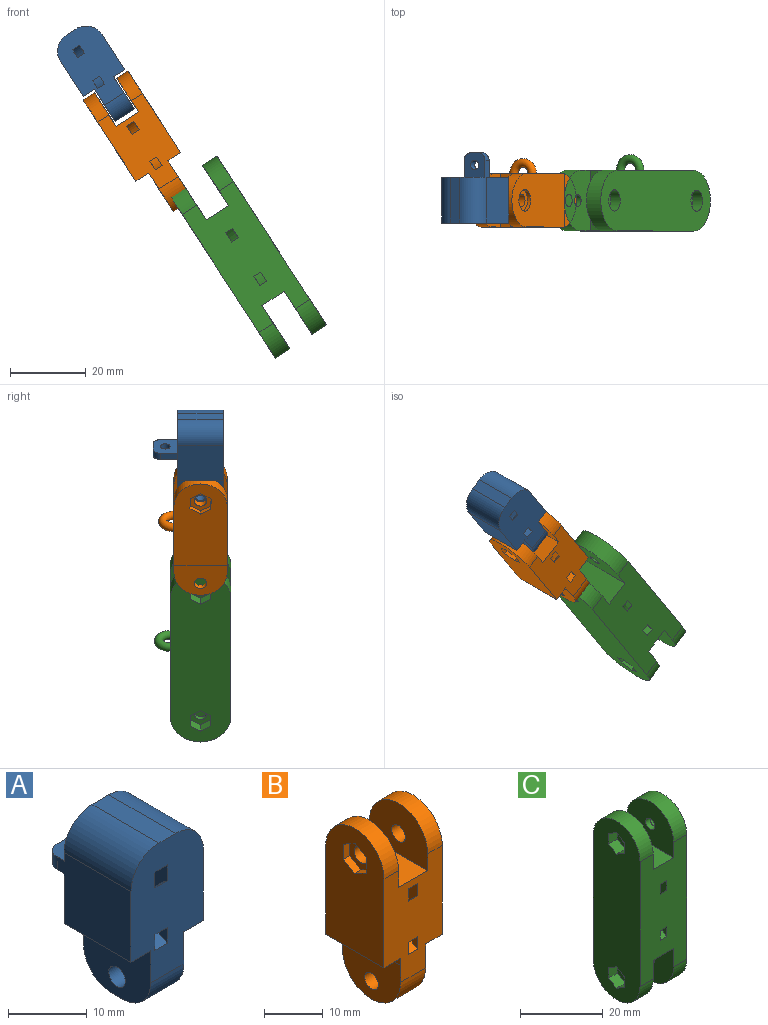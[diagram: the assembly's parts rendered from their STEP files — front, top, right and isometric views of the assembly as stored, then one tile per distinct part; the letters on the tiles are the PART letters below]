
ASSEMBLY  parts=3 mates=1
PART A: 27 faces, bbox 13x18.5x26 mm
  f0: plane 21x13mm, normal (0,-1,0), area 216.5mm2, adj f3,f4,f5,f6,f7,f8,f9,f11
  f1: plane 6x2mm, normal (0,0,-1), area 12mm2, adj f6,f9,f13,f14
  f2: plane 21x13mm, normal (0,1,0), area 214.3mm2, adj f3,f4,f5,f6,f7,f8,f9,f11
  f3: plane 12x11mm, normal (1,0,0), area 132mm2, adj f0,f2,f8,f12
  f4: plane 12x11mm, normal (-1,0,0), area 132mm2, adj f0,f2,f7,f11
  f5: plane 12x3mm, normal (0,0,1), area 36mm2, adj f0,f2,f11,f12
  f6: plane 12x10mm, normal (-1,0,0), area 102.2mm2, adj f0,f1,f2,f7,f10,f13,f14
  f7: plane 12x3.5mm, normal (0,0,-1), area 42mm2, adj f0,f2,f4,f6
  f8: plane 12x3.5mm, normal (0,0,-1), area 42mm2, adj f0,f2,f3,f9
  f9: plane 12x10mm, normal (1,0,0), area 102.2mm2, adj f0,f1,f2,f8,f10,f13,f14
  f10: cylinder r=1.5mm len=6mm, axis (-1,0,0), area 56.5mm2, adj f6,f9
  f11: cylinder r=5mm len=12mm, axis (0,-1,0), area 94.2mm2, adj f0,f2,f4,f5
  f12: cylinder r=5mm len=12mm, axis (0,1,0), area 94.2mm2, adj f0,f2,f3,f5
  f13: cylinder r=5mm len=6mm, axis (1,0,0), area 47.1mm2, adj f1,f2,f6,f9
  f14: cylinder r=5mm len=6mm, axis (1,0,0), area 47.1mm2, adj f0,f1,f6,f9
  f15: plane 6.5x6.5mm, normal (0,0,-1), area 35.6mm2, adj f2,f16,f18,f19,f20,f21,f22
  f16: plane 4.5x2mm, normal (-1,0,0), area 9mm2, adj f2,f15,f17,f22
  f17: plane 6.5x6.5mm, normal (0,0,1), area 35.6mm2, adj f2,f16,f18,f19,f20,f21,f22
  f18: plane 4.5x2mm, normal (1,0,0), area 9mm2, adj f2,f15,f17,f21
  f19: plane 2.5x2mm, normal (0,1,0), area 5mm2, adj f15,f17,f21,f22
  f20: cylinder r=1.25mm len=2.5mm, axis (0,0,-1), area 15.7mm2, adj f15,f17
  f21: cylinder r=2mm len=2mm, axis (0,0,1), area 6.3mm2, adj f15,f17,f18,f19
  f22: cylinder r=2mm len=2mm, axis (0,0,-1), area 6.3mm2, adj f15,f16,f17,f19
  f23: cylinder r=6.5mm len=12.16mm, axis (1,0,0), area 34.6mm2, adj f0,f25,f26
  f24: cylinder r=4.3mm len=7.27mm, axis (1,0,0), area 19mm2, adj f0,f25,f26
  f25: plane 12.16x4.2mm, normal (1,0,0), area 26.8mm2, adj f0,f23,f24
  f26: plane 12.16x4.2mm, normal (-1,0,0), area 26.8mm2, adj f0,f23,f24
PART B: 33 faces, bbox 14x18.3x37.5 mm
  f0: plane 25.49x14mm, normal (-1,0,0), area 309.6mm2, adj f11,f13,f14,f16,f22,f23,f24,f25
  f1: cylinder r=1.65mm len=3.3mm, axis (1,0,0), area 20.7mm2, adj f10,f21
  f2: cylinder r=1.65mm len=3.3mm, axis (1,0,0), area 25.9mm2, adj f8,f19
  f3: plane 14x10.5mm, normal (-1,0,0), area 117.4mm2, adj f12,f13,f14,f15,f18
  f4: plane 14x10.47mm, normal (1,0,0), area 117mm2, adj f5,f13,f14,f15,f18
  f5: plane 14x1.5mm, normal (1,0,-0.01), area 21mm2, adj f4,f6,f13,f14
  f6: plane 14x4mm, normal (0,0,-1), area 56mm2, adj f5,f7,f13,f14
  f7: plane 25.52x14mm, normal (1,0,0), area 310.8mm2, adj f6,f13,f14,f17,f20
  f8: plane 14x10.51mm, normal (-1,0,0), area 117.5mm2, adj f2,f9,f13,f14,f17
  f9: plane 14x7mm, normal (0,0,1), area 98mm2, adj f8,f10,f13,f14
  f10: plane 14x10.51mm, normal (1,0,0), area 117.5mm2, adj f1,f9,f13,f14,f16
  f11: plane 14x4mm, normal (0,0,-1), area 56mm2, adj f0,f12,f13,f14
  f12: plane 14x1.5mm, normal (-1,0,0.01), area 21mm2, adj f3,f11,f13,f14
  f13: plane 23.49x14mm, normal (0,-1,0), area 253.3mm2, adj f0,f3,f4,f5,f6,f7,f8,f9
  f14: plane 23.49x14mm, normal (0,1,0), area 256.5mm2, adj f0,f3,f4,f5,f6,f7,f8,f9
  f15: cylinder r=1.65mm len=6mm, axis (1,0,0), area 62.2mm2, adj f3,f4
  f16: cylinder r=7mm len=14mm, axis (1,0,0), area 77mm2, adj f0,f10,f13,f14
  f17: cylinder r=7mm len=14mm, axis (1,0,0), area 77mm2, adj f7,f8,f13,f14
  f18: cylinder r=7mm len=14mm, axis (-1,0,0), area 131.9mm2, adj f3,f4,f13,f14
  f19: plane 5.7x5.7mm, normal (1,0,0), area 17mm2, adj f2,f20
  f20: cylinder r=2.85mm len=5.7mm, axis (1,0,0), area 17.9mm2, adj f7,f19
  f21: plane 6.35x5.57mm, normal (-1,0,0), area 17.7mm2, adj f1,f22,f23,f24,f25,f26,f27
  f22: plane 3.18x1.5mm, normal (0,1,0.02), area 4.8mm2, adj f0,f21,f23,f27
  f23: plane 2.72x1.65mm, normal (0,0.52,-0.86), area 4.8mm2, adj f0,f21,f22,f24
  f24: plane 2.78x1.53mm, normal (0,-0.48,-0.88), area 4.8mm2, adj f0,f21,f23,f25
  f25: plane 3.18x1.5mm, normal (0,-1,-0.02), area 4.8mm2, adj f0,f21,f24,f26
  f26: plane 2.72x1.65mm, normal (0,-0.52,0.86), area 4.8mm2, adj f0,f21,f25,f27
  f27: plane 2.78x1.53mm, normal (0,0.48,0.88), area 4.8mm2, adj f0,f21,f22,f26
  f28: torus R=2.89mm, axis (0,0,1), area 64.2mm2, adj f14
  f29: cylinder r=7.5mm len=13.66mm, axis (1,0,0), area 37.8mm2, adj f13,f31,f32
  f30: cylinder r=5.3mm len=8.6mm, axis (1,0,0), area 22.1mm2, adj f13,f31,f32
  f31: plane 13.66x4.4mm, normal (1,0,0), area 30mm2, adj f13,f29,f30
  f32: plane 13.66x4.4mm, normal (-1,0,0), area 30mm2, adj f13,f29,f30
PART C: 41 faces, bbox 16x20.5x53 mm
  f0: plane 53x16mm, normal (-1,0,0), area 740.7mm2, adj f12,f13,f16,f17,f22,f23,f24,f25
  f1: cylinder r=1.55mm len=3.1mm, axis (1,0,0), area 14.6mm2, adj f11,f29
  f2: cylinder r=1.55mm len=3.1mm, axis (1,0,0), area 14.6mm2, adj f6,f28
  f3: plane 53x16mm, normal (1,0,0), area 743.8mm2, adj f12,f13,f14,f15,f18,f21
  f4: cylinder r=1.55mm len=3.1mm, axis (1,0,0), area 14.6mm2, adj f9,f20
  f5: cylinder r=1.55mm len=3.1mm, axis (1,0,0), area 14.6mm2, adj f8,f19
  f6: plane 16x13.5mm, normal (1,0,0), area 181mm2, adj f2,f7,f12,f13,f16
  f7: plane 16x7mm, normal (0,0,-1), area 112mm2, adj f6,f8,f12,f13
  f8: plane 16x13.5mm, normal (-1,0,0), area 181mm2, adj f5,f7,f12,f13,f15
  f9: plane 16x12.59mm, normal (-1,0,0), area 166.5mm2, adj f4,f10,f12,f13,f14
  f10: plane 16x7mm, normal (0,0,1), area 112mm2, adj f9,f11,f12,f13
  f11: plane 16x12.59mm, normal (1,0,0), area 166.5mm2, adj f1,f10,f12,f13,f17
  f12: plane 37x16mm, normal (0,-1,0), area 508.8mm2, adj f0,f3,f6,f7,f8,f9,f10,f11
  f13: plane 37x16mm, normal (0,1,0), area 513.4mm2, adj f0,f3,f6,f7,f8,f9,f10,f11
  f14: cylinder r=8mm len=16mm, axis (1,0,0), area 113.1mm2, adj f3,f9,f12,f13
  f15: cylinder r=8mm len=16mm, axis (-1,0,0), area 113.1mm2, adj f3,f8,f12,f13
  f16: cylinder r=8mm len=16mm, axis (-1,0,0), area 113.1mm2, adj f0,f6,f12,f13
  f17: cylinder r=8mm len=16mm, axis (1,0,0), area 113.1mm2, adj f0,f11,f12,f13
  f18: cylinder r=2.8mm len=5.6mm, axis (1,0,0), area 52.8mm2, adj f3,f19
  f19: plane 5.6x5.6mm, normal (1,0,0), area 17.1mm2, adj f5,f18
  f20: plane 5.6x5.6mm, normal (1,0,0), area 17.1mm2, adj f4,f21
  f21: cylinder r=2.8mm len=5.6mm, axis (1,0,0), area 52.8mm2, adj f3,f20
  f22: plane 3x2.75mm, normal (0,0.5,-0.87), area 9.5mm2, adj f0,f23,f27,f28
  f23: plane 3x2.75mm, normal (0,-0.5,-0.87), area 9.5mm2, adj f0,f22,f24,f28
  f24: plane 3.18x3mm, normal (0,-1,0), area 9.5mm2, adj f0,f23,f25,f28
  f25: plane 3x2.75mm, normal (0,-0.5,0.87), area 9.5mm2, adj f0,f24,f26,f28
  f26: plane 3x2.75mm, normal (0,0.5,0.87), area 9.5mm2, adj f0,f25,f27,f28
  f27: plane 3.18x3mm, normal (0,1,0), area 9.5mm2, adj f0,f22,f26,f28
  f28: plane 6.35x5.5mm, normal (-1,0,0), area 18.6mm2, adj f2,f22,f23,f24,f25,f26,f27
  f29: plane 6.35x5.5mm, normal (-1,0,0), area 18.6mm2, adj f1,f30,f31,f32,f33,f34,f35
  f30: plane 3x2.75mm, normal (0,0.5,-0.87), area 9.5mm2, adj f0,f29,f31,f35
  f31: plane 3x2.75mm, normal (0,-0.5,-0.87), area 9.5mm2, adj f0,f29,f30,f32
  f32: plane 3.18x3mm, normal (0,-1,0), area 9.5mm2, adj f0,f29,f31,f33
  f33: plane 3x2.75mm, normal (0,-0.5,0.87), area 9.5mm2, adj f0,f29,f32,f34
  f34: plane 3x2.75mm, normal (0,0.5,0.87), area 9.5mm2, adj f0,f29,f33,f35
  f35: plane 3.18x3mm, normal (0,1,0), area 9.5mm2, adj f0,f29,f30,f34
  f36: torus R=3mm, axis (0,0,1), area 66.6mm2, adj f13
  f37: cylinder r=7.8mm len=10.86mm, axis (1,0,0), area 26.4mm2, adj f12,f39,f40
  f38: cylinder r=10mm len=16.57mm, axis (1,0,0), area 43mm2, adj f12,f39,f40
  f39: plane 16.57x4.4mm, normal (1,0,0), area 34.8mm2, adj f12,f37,f38
  f40: plane 16.57x4.4mm, normal (-1,0,0), area 34.8mm2, adj f12,f37,f38
PLACE A rot(axis=(0,-1,0),32.9deg) t=(-14.31,-7.12,59.36)mm
PLACE B rot(axis=(0,-1,0),32.9deg) t=(27.51,-7.12,54.56)mm
PLACE C rot(axis=(0,-1,0),33deg) t=(24.44,0.88,11.51)mm
MATE revolute A.f10 <-> B.f1  axis (-0.84,0,-0.54) through (-6.65,-7.12,53.04)mm
